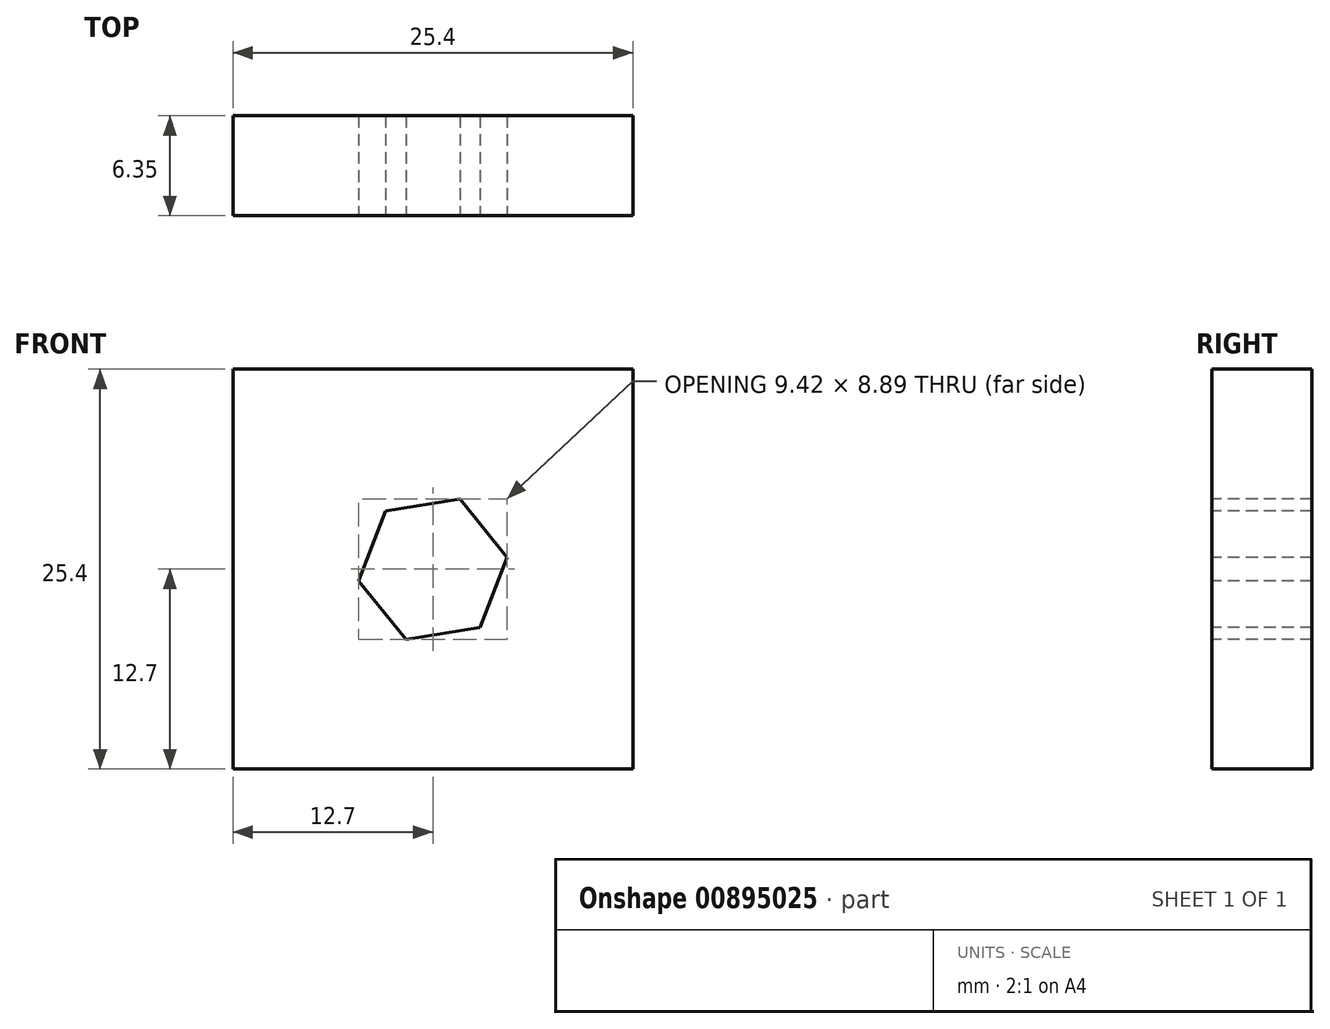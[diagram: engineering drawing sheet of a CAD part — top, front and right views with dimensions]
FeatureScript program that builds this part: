
annotation { "Feature Type Name" : "Feature", "Feature Type Description" : "" }
export const myFeature = defineFeature(function(context is Context, id is Id, definition is map)
    precondition{}
    {
        {
            var Q0;
            Q0=qCreatedBy(makeId("Top.planeOp"),FACE);
            var sketch = newSketch(context, id + "F0", { "sketchPlane" : qUnion([Q0])});
            skLineSegment(sketch, "E0.bottom", {"start": v(-2.89, 16.43) * mm, "end": v(22.51, 16.43) * mm});
            skLineSegment(sketch, "E0.top", {"start": v(-2.89, 10.08) * mm, "end": v(22.51, 10.08) * mm});
            skLineSegment(sketch, "E0.left", {"start": v(-2.89, 16.43) * mm, "end": v(-2.89, 10.08) * mm});
            skLineSegment(sketch, "E0.right", {"start": v(22.51, 16.43) * mm, "end": v(22.51, 10.08) * mm});
            skSolve(sketch);
        }
        {
            var Q0;
            Q0=qSketchRegion(id+"F0",true);
            extrude(context, id + "F1", {"entities" : qUnion([Q0]), "depth" : 25.4 * mm, "offsetDistance" : 25.4 * mm});
        }
        {
            var Q0;
            Q0=makeQuery(id+"F1.opExtrude","SWEPT_FACE",FACE,{"disambiguationData":[OSD([sQuery(id+"F0.wireOp",EDGE,"E0.top")])]});
            var sketch = newSketch(context, id + "F2", { "sketchPlane" : qUnion([Q0])});
            skCircle(sketch, "E1", {"center": v(9.81, 12.7) * mm, "radius": 4.13 * mm});
            skPoint(sketch, "E1.centerSnap0", {"position": v(9.81, 25.4) * mm});
            skCircle(sketch, "E2.cCircle", {"center": v(9.81, 12.7) * mm, "radius": 4.13 * mm, "construction": true});
            skLineSegment(sketch, "E2.0", {"start": v(14.52, 13.44) * mm, "end": v(12.8, 9) * mm});
            skLineSegment(sketch, "E2.1", {"start": v(12.8, 9) * mm, "end": v(8.1, 8.25) * mm});
            skLineSegment(sketch, "E2.2", {"start": v(8.1, 8.25) * mm, "end": v(5.1, 11.96) * mm});
            skLineSegment(sketch, "E2.3", {"start": v(5.1, 11.96) * mm, "end": v(6.82, 16.4) * mm});
            skLineSegment(sketch, "E2.4", {"start": v(6.82, 16.4) * mm, "end": v(11.52, 17.15) * mm});
            skLineSegment(sketch, "E2.5", {"start": v(11.52, 17.15) * mm, "end": v(14.52, 13.44) * mm});
            skPoint(sketch, "E2.0.midPoint", {"position": v(13.66, 11.22) * mm});
            skSolve(sketch);
        }
        {
            var Q0;
            Q0=qSketchRegion(id+"F2",true);
            extrude(context, id + "F3", {"entities" : qUnion([Q0]), "operationType" : NewBodyOperationType.REMOVE, "oppositeDirection" : true, "depth" : 25.4 * mm, "offsetDistance" : 25.4 * mm});
        }
    });
